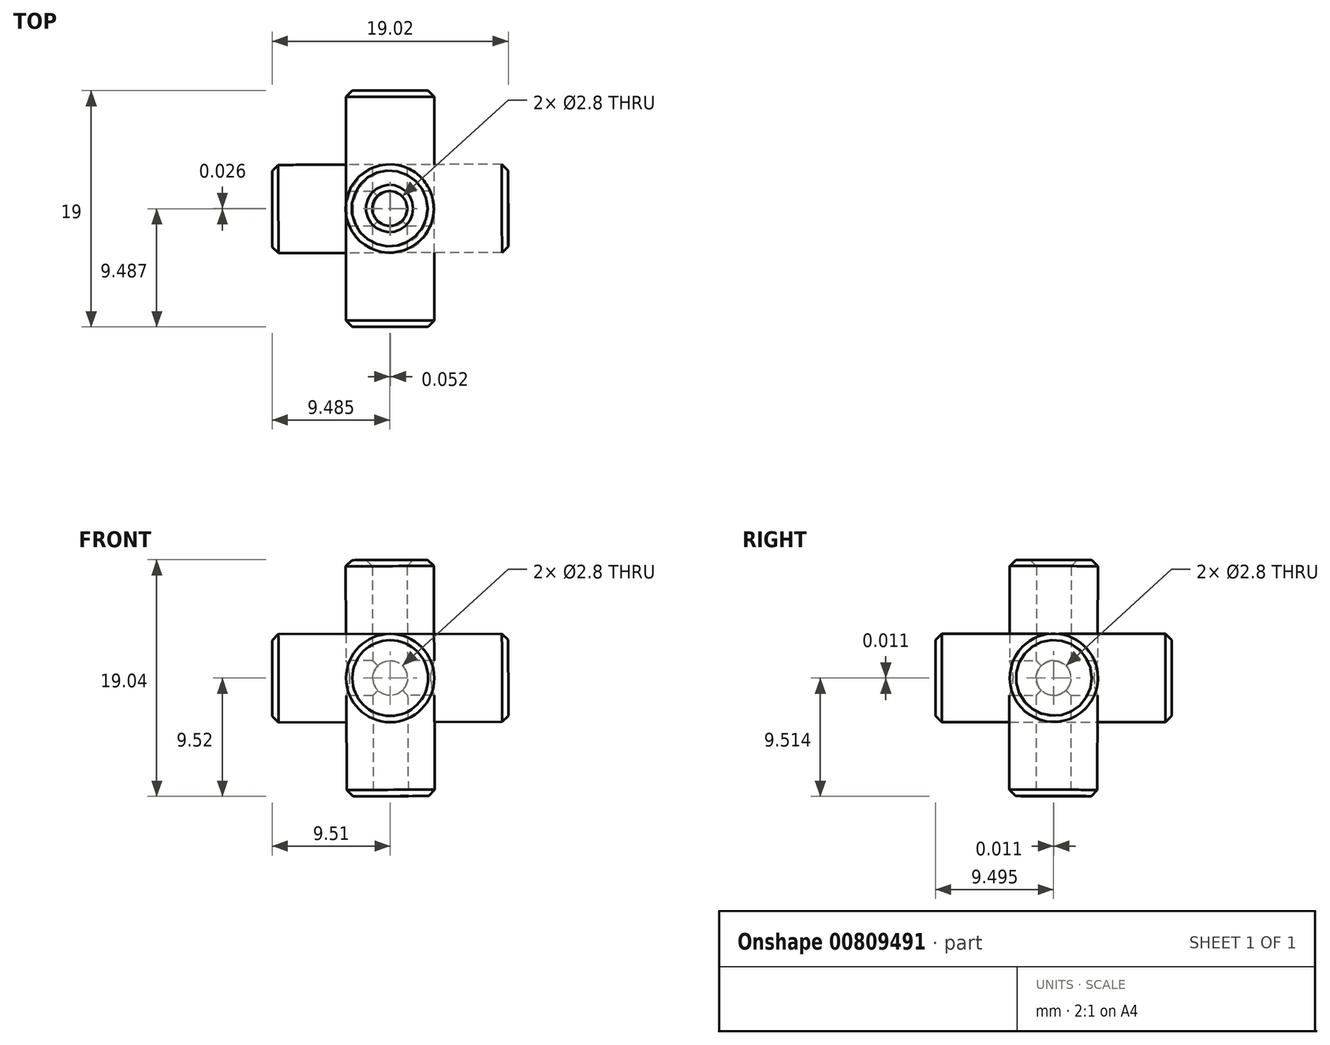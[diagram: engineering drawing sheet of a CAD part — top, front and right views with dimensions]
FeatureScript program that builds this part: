
annotation { "Feature Type Name" : "Feature", "Feature Type Description" : "" }
export const myFeature = defineFeature(function(context is Context, id is Id, definition is map)
    precondition{}
    {
        {
            var Q0;
            Q0=qCreatedBy(makeId("Front.planeOp"),FACE);
            var sketch = newSketch(context, id + "F0", { "sketchPlane" : qUnion([Q0])});
            skCircle(sketch, "E0", {"center": v(0, 0) * mm, "radius": 3.55 * mm});
            skSolve(sketch);
        }
        {
            var Q0;
            Q0=makeQuery(id+"F0.imprint","IMPRINT",FACE,{"disambiguationData":[TD([[makeQuery(id+"F0.imprint","IMPRINT",EDGE,{"derivedFrom":sQuery(id+"F0.wireOp",EDGE,"E0")}),1.0]])]});
            extrude(context, id + "F1", {"entities" : qUnion([Q0]), "endBound" : BoundingType.SYMMETRIC, "depth" : 19 * mm, "offsetDistance" : 25 * mm});
        }
        {
            var Q0;
            Q0=qCreatedBy(makeId("Front.planeOp"),FACE);
            var sketch = newSketch(context, id + "F2", { "sketchPlane" : qUnion([Q0])});
            skCircle(sketch, "E1", {"center": v(0, 0) * mm, "radius": 1.4 * mm});
            skSolve(sketch);
        }
        {
            var Q0;
            Q0 = qSketchRegion(id + "F2", true);
            extrude(context, id + "F3", {"entities" : qUnion([Q0]), "endBound" : BoundingType.SYMMETRIC, "depth" : 20 * mm, "offsetDistance" : 25 * mm});
        }
        {
            var Q0;
            Q0=qCreatedBy(makeId("Front.planeOp"),FACE);
            var sketch = newSketch(context, id + "F4", { "sketchPlane" : qUnion([Q0])});
            skLineSegment(sketch, "E2.bottom", {"start": v(0, 0.08) * mm, "end": v(10, 0.08) * mm});
            skLineSegment(sketch, "E2.top", {"start": v(0, 10.08) * mm, "end": v(10, 10.08) * mm});
            skLineSegment(sketch, "E2.left", {"start": v(0, 0.08) * mm, "end": v(0, 10.08) * mm});
            skLineSegment(sketch, "E2.right", {"start": v(10, 0.08) * mm, "end": v(10, 10.08) * mm});
            skSolve(sketch);
        }
        {
            var Q0;
            Q0 = qSketchRegion(id + "F4", true);
            extrude(context, id + "F5", {"entities" : qUnion([Q0]), "depth" : 10 * mm, "offsetDistance" : 25 * mm});
        }
        {
            var Q0;
            Q0=qCreatedBy(makeId("Origin.pointOp"),VERTEX);
            var Q1;
            Q1=makeQuery(id+"F5.opExtrude","CAP_VERTEX",VERTEX,{"disambiguationData":[OSD([sQuery(id+"F4.wireOp",EDGE,"E2.top"),sQuery(id+"F4.wireOp",EDGE,"E2.right")])],"isStart":false});
            var Q2;
            Q2=makeQuery(id+"F5.opExtrude","CAP_VERTEX",VERTEX,{"disambiguationData":[OSD([sQuery(id+"F4.wireOp",EDGE,"E2.bottom"),sQuery(id+"F4.wireOp",EDGE,"E2.right")])],"isStart":false});
            cPlane(context, id + "F6", {"entities" : qUnion([Q0, Q1, Q2]), "cplaneType" : CPlaneType.THREE_POINT, "offset" : 25 * mm, "width" : 150 * mm, "height" : 150 * mm});
        }
        {
            var Q0;
            Q0=qCreatedBy(id+"F6.planeOp",FACE);
            var sketch = newSketch(context, id + "F7", { "sketchPlane" : qUnion([Q0])});
            skLineSegment(sketch, "E3", {"start": v(0, 0) * mm, "end": v(14.14, 10.08) * mm});
            skSolve(sketch);
        }
        {
            var Q0;
            Q0=makeQuery(id+"F5.opExtrude","SWEPT_BODY",BODY,{"disambiguationData":[OSD([sQuery(id+"F4.wireOp",EDGE,"E2.bottom"),sQuery(id+"F4.wireOp",EDGE,"E2.top"),sQuery(id+"F4.wireOp",EDGE,"E2.left"),sQuery(id+"F4.wireOp",EDGE,"E2.right")])]});
            deleteBodies(context, id + "F8", {"entities" : qUnion([Q0])});
        }
        {
            var Q0;
            Q0=makeQuery(id+"F1.opExtrude","SWEPT_BODY",BODY,{"disambiguationData":[OSD([sQuery(id+"F0.wireOp",EDGE,"E0")])]});
            var Q1;
            Q1=makeQuery(id+"F3.opExtrude","SWEPT_BODY",BODY,{"disambiguationData":[OSD([sQuery(id+"F2.wireOp",EDGE,"E1")])]});
            var Q2;
            Q2=sQuery(id+"F7.wireOp",EDGE,"E3");
            circularPattern(context, id + "F9", {"entities" : qUnion([Q0, Q1]), "axis" : qUnion([Q2]), "angle" : 360 * degree, "instanceCount" : 3, "equalSpace" : true});
        }
        {
            var Q0;
            Q0=makeQuery(id+"F9.opPattern","COPY",BODY,{"derivedFrom":makeQuery(id+"F3.opExtrude","SWEPT_BODY",BODY,{"disambiguationData":[OSD([sQuery(id+"F2.wireOp",EDGE,"E1")])]}),"instanceName":"1"});
            var Q1;
            Q1=makeQuery(id+"F3.opExtrude","SWEPT_BODY",BODY,{"disambiguationData":[OSD([sQuery(id+"F2.wireOp",EDGE,"E1")])]});
            var Q2;
            Q2=makeQuery(id+"F9.opPattern","COPY",BODY,{"derivedFrom":makeQuery(id+"F3.opExtrude","SWEPT_BODY",BODY,{"disambiguationData":[OSD([sQuery(id+"F2.wireOp",EDGE,"E1")])]}),"instanceName":"2"});
            var Q3;
            Q3=makeQuery(id+"F9.opPattern","COPY",BODY,{"derivedFrom":makeQuery(id+"F1.opExtrude","SWEPT_BODY",BODY,{"disambiguationData":[OSD([sQuery(id+"F0.wireOp",EDGE,"E0")])]}),"instanceName":"2"});
            booleanBodies(context, id + "F10", {"operationType" : BooleanOperationType.SUBTRACTION, "tools" : qUnion([Q0, Q1, Q2]), "targets" : qUnion([Q3])});
        }
        {
            var Q0;
            Q0=makeQuery(id+"F1.opExtrude","CAP_FACE",FACE,{"disambiguationData":[OSD([sQuery(id+"F0.wireOp",EDGE,"E0")])],"isStart":true});
            var Q1;
            Q1=makeQuery(id+"F10.opBoolean","INTERSECT",EDGE,{"derivedFrom":[makeQuery(id+"F9.opPattern","COPY",FACE,{"derivedFrom":makeQuery(id+"F1.opExtrude","CAP_FACE",FACE,{"disambiguationData":[OSD([sQuery(id+"F0.wireOp",EDGE,"E0")])],"isStart":false}),"instanceName":"1"}),makeQuery(id+"F9.opPattern","COPY",FACE,{"derivedFrom":makeQuery(id+"F3.opExtrude","SWEPT_FACE",FACE,{"disambiguationData":[OSD([sQuery(id+"F2.wireOp",EDGE,"E1")])]}),"instanceName":"1"})]});
            var Q2;
            Q2=makeQuery(id+"F1.opExtrude","CAP_EDGE",EDGE,{"disambiguationData":[OSD([sQuery(id+"F0.wireOp",EDGE,"E0")])],"isStart":false});
            var Q3;
            Q3=makeQuery(id+"F9.opPattern","COPY",EDGE,{"derivedFrom":makeQuery(id+"F1.opExtrude","CAP_EDGE",EDGE,{"disambiguationData":[OSD([sQuery(id+"F0.wireOp",EDGE,"E0")])],"isStart":true}),"instanceName":"2"});
            var Q4;
            Q4=makeQuery(id+"F9.opPattern","COPY",FACE,{"derivedFrom":makeQuery(id+"F1.opExtrude","CAP_FACE",FACE,{"disambiguationData":[OSD([sQuery(id+"F0.wireOp",EDGE,"E0")])],"isStart":false}),"instanceName":"2"});
            var Q5;
            Q5=makeQuery(id+"F9.opPattern","COPY",FACE,{"derivedFrom":makeQuery(id+"F1.opExtrude","CAP_FACE",FACE,{"disambiguationData":[OSD([sQuery(id+"F0.wireOp",EDGE,"E0")])],"isStart":true}),"instanceName":"1"});
            var Q6;
            Q6=makeQuery(id+"F9.opPattern","COPY",FACE,{"derivedFrom":makeQuery(id+"F1.opExtrude","CAP_FACE",FACE,{"disambiguationData":[OSD([sQuery(id+"F0.wireOp",EDGE,"E0")])],"isStart":false}),"instanceName":"1"});
            chamfer(context, id + "F11", {"entities" : qUnion([Q0, Q1, Q2, Q3, Q4, Q5, Q6]), "width" : 0.5 * mm, "tangentPropagation" : true});
        }
    });
